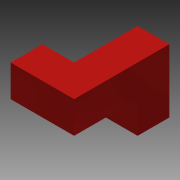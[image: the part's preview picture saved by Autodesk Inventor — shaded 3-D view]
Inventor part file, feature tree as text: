
AUTODESK INVENTOR PART (.ipt)
format: ipt  version: 2015 (Build 190159000, 159)  size: 102,400 bytes
history: native  units: in
note: dims shown in document units (in); Inventor stores cm internally (conversion verified against a paired STEP export)
features: extrude x3, sketch x3
ambient origin geometry x8: Origin, YZ Plane, XZ Plane, XY Plane, X Axis, Y Axis, Z Axis, Center Point
bodies: Solid1 (feature_tree)
feature tree (6):
  extrude  "Extrusion1"  Depth=0.75in
  extrude  "Extrusion2"  Depth=0.75in
  extrude  "Extrusion3"  Depth=0.75in TaperAngle=0.0deg
  sketch  "Sketch1"  dims[d0=1.5in d1=0.75in]
  sketch  "Sketch2"  dims[d2=2.25in d3=0.75in]
  sketch  "Sketch3"  dims[d4=1.5in d5=0.75in d6=0.0in d7=0.75in d8=0.0in d9=0.75in d10=0.75in d11=0.0in]
